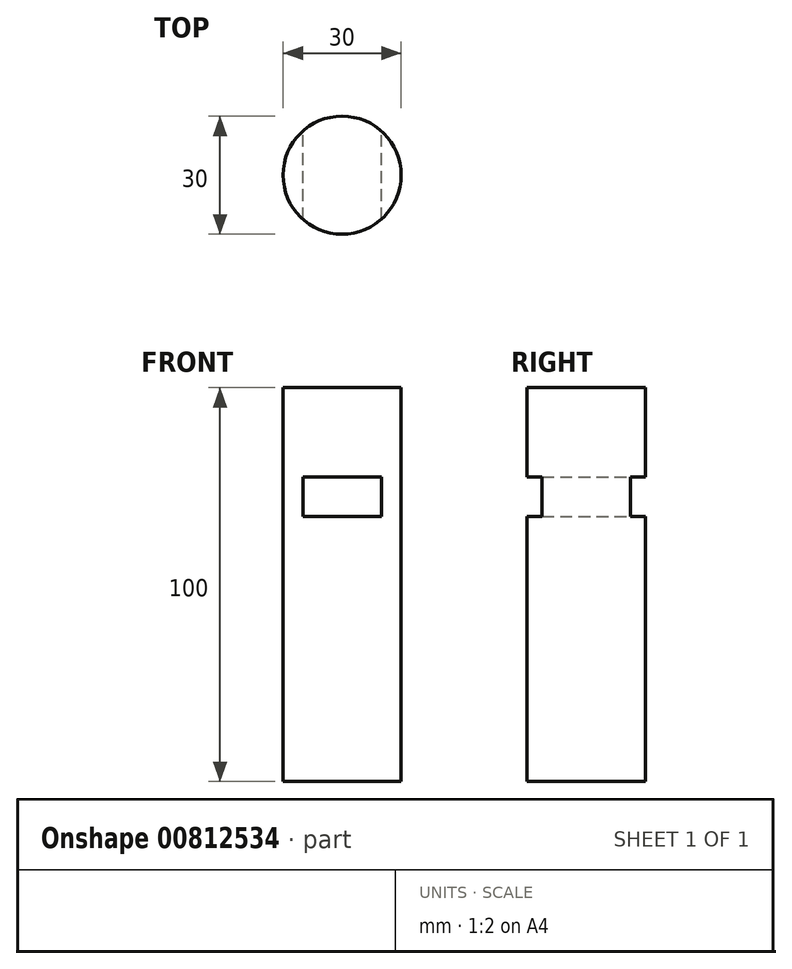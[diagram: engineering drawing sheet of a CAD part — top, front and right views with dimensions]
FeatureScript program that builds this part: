
annotation { "Feature Type Name" : "Feature", "Feature Type Description" : "" }
export const myFeature = defineFeature(function(context is Context, id is Id, definition is map)
    precondition{}
    {
        {
            var Q0;
            Q0=qCreatedBy(makeId("Top.planeOp"),FACE);
            var sketch = newSketch(context, id + "F0", { "sketchPlane" : qUnion([Q0])});
            skCircle(sketch, "E0", {"center": v(0, 0) * mm, "radius": 15 * mm});
            skSolve(sketch);
        }
        {
            var Q0;
            Q0=makeQuery(id+"F0.imprint","IMPRINT",FACE,{"disambiguationData":[TD([[makeQuery(id+"F0.imprint","IMPRINT",EDGE,{"derivedFrom":sQuery(id+"F0.wireOp",EDGE,"E0")}),1.0]])]});
            extrude(context, id + "F1", {"entities" : qUnion([Q0]), "depth" : 100 * mm, "offsetDistance" : 25 * mm});
        }
        {
            var Q0;
            Q0=qCreatedBy(makeId("Front.planeOp"),FACE);
            var sketch = newSketch(context, id + "F2", { "sketchPlane" : qUnion([Q0])});
            skLineSegment(sketch, "E1.bottom", {"start": v(-10, 77.27) * mm, "end": v(10, 77.27) * mm});
            skLineSegment(sketch, "E1.top", {"start": v(-10, 67.27) * mm, "end": v(10, 67.27) * mm});
            skLineSegment(sketch, "E1.left", {"start": v(-10, 77.27) * mm, "end": v(-10, 67.27) * mm});
            skLineSegment(sketch, "E1.right", {"start": v(10, 77.27) * mm, "end": v(10, 67.27) * mm});
            skSolve(sketch);
        }
        {
            var Q0;
            Q0 = qSketchRegion(id + "F2", true);
            extrude(context, id + "F3", {"entities" : qUnion([Q0]), "operationType" : NewBodyOperationType.REMOVE, "endBound" : BoundingType.SYMMETRIC, "depth" : 150 * mm, "offsetDistance" : 25 * mm});
        }
    });
